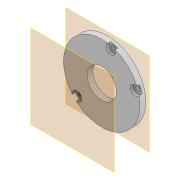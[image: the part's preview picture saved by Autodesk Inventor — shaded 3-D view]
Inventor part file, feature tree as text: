
AUTODESK INVENTOR PART (.ipt)
format: ipt  version: 2022 (Build 260153000, 153)  size: 178,176 bytes
history: native  units: in
note: dims shown in document units (in); Inventor stores cm internally (conversion verified against a paired STEP export)
features: sketch x5, reference x5, extrude x4, other x4, plane x2, hole x1, pattern_circular x1, projected_geometry x1
ambient origin geometry x8: Origin, YZ Plane, XZ Plane, XY Plane, X Axis, Y Axis, Z Axis, Center Point
bodies: Solid1 (feature_tree)
feature tree (23):
  plane  "Work Plane1"
  extrude  "Extrusion1"  Depth=0.0787in
  hole  "Bohrung1"  [1 undecoded]
  plane  "Arbeitsebene3"
  extrude  "Extrusion13"  TaperAngle=135.0deg  [1 undecoded]
  extrude  "Extrusion14"  Depth=0.3937in
  extrude  "Extrusion15"  Depth=0.3937in
  pattern_circular  "Runde Anordnung1"  [2 undecoded]
  sketch  "Sketch1"  dims[d0=0.1575in d1=0.0in]
  reference  "Reference1"
  reference  "Reference5"
  reference  "Reference6"
  reference  "Reference7"
  sketch  "Skizze4"  dims[d9=0.126in d10=0.75in d11=0.2559in d12=0.0787in d13=0.5635in d14=1.0in d15=0.8108in d17=0.7874in]
  reference  "Referenz9"
  sketch  "Skizze19"  dims[d64=0.7874in d65=0.7756in]
  sketch  "Skizze20"  dims[d66=1.063in d67=135.0deg]
  sketch  "Skizze21"  dims[d68=135.0deg d69=0.1181in d70=0.1181in d71=0.2756in d72=0.0in d73=0.2362in d74=0.2756in d75=0.0in d76=0.1102in d77=0.3937in d78=0.0in d79=1.1811in d80=180.0deg]
  projected_geometry  "Projizierte Kontur11"
  other  "<userpath>\Documents\Matchboxscope\INVENTOR\Matchboxscope_v1.iam"
  other  "Matchboxscope_v1.iam"
  other  "Matchboxscope_middle2_v1:1"
  other  "Matchboxscope_middle2_v2:1"
note: 4 required parameter values undecoded (feature->parameter linkage not recoverable at this tier; creation-order binding heuristic only, values carry confidence <= 0.55)
